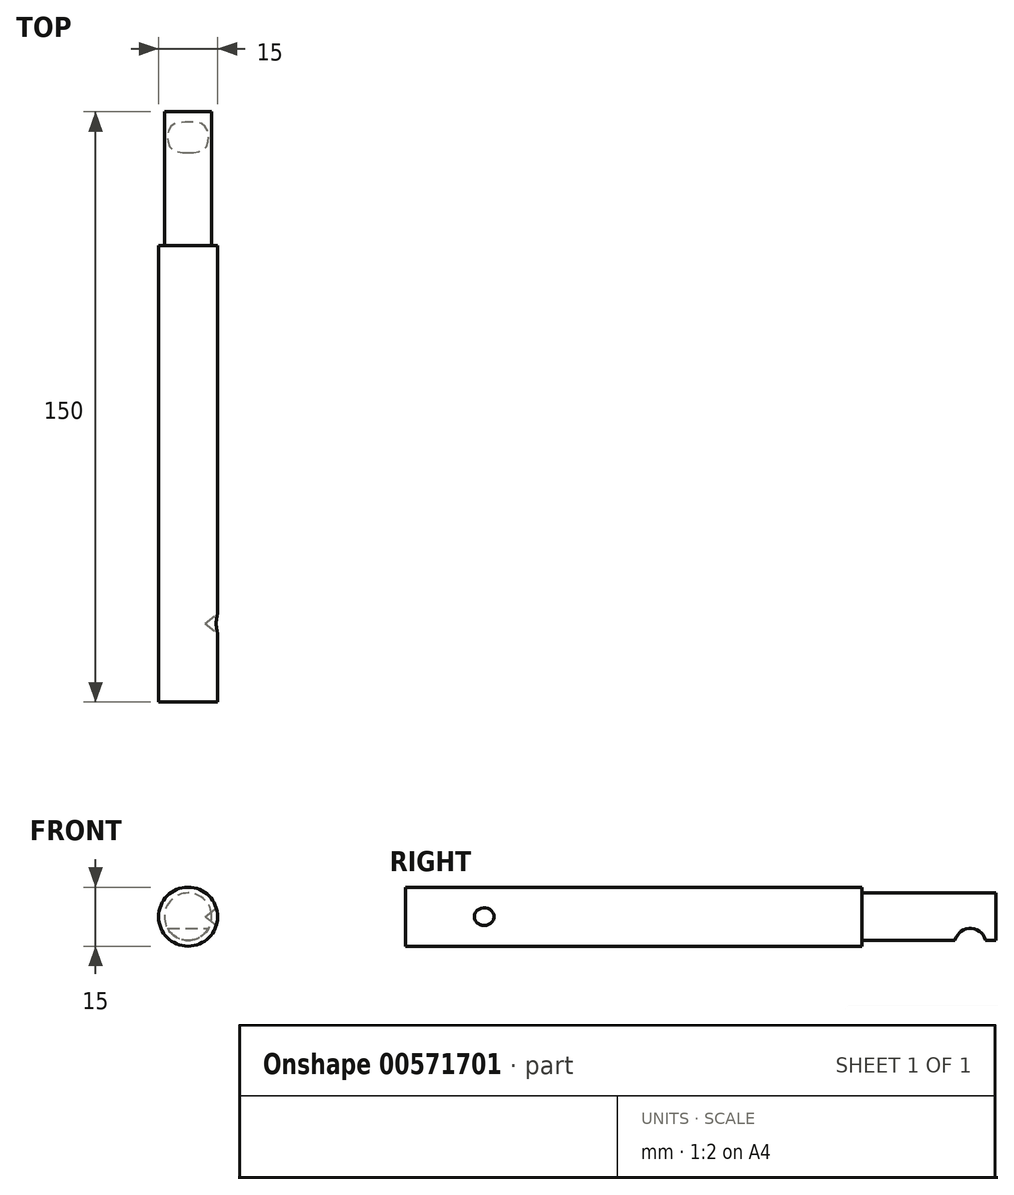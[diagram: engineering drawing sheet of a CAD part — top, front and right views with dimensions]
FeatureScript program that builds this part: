
annotation { "Feature Type Name" : "Feature", "Feature Type Description" : "" }
export const myFeature = defineFeature(function(context is Context, id is Id, definition is map)
    precondition{}
    {
        {
            var Q0;
            Q0=qCreatedBy(makeId("Top.planeOp"),FACE);
            var sketch = newSketch(context, id + "F0", { "sketchPlane" : qUnion([Q0])});
            skLineSegment(sketch, "E0", {"start": v(0, 0) * mm, "end": v(0, 150) * mm, "construction": true});
            skLineSegment(sketch, "E1", {"start": v(0, 0) * mm, "end": v(-7.5, 0) * mm});
            skLineSegment(sketch, "E2", {"start": v(-7.5, 0) * mm, "end": v(-7.5, 116) * mm});
            skLineSegment(sketch, "E3", {"start": v(-6, 116) * mm, "end": v(-6, 150) * mm});
            skLineSegment(sketch, "E4", {"start": v(-6, 150) * mm, "end": v(0, 150) * mm});
            skLineSegment(sketch, "E5", {"start": v(-6, 116) * mm, "end": v(-7.5, 116) * mm});
            skLineSegment(sketch, "E6", {"start": v(0, 150) * mm, "end": v(0, 0) * mm});
            skSolve(sketch);
        }
        {
            var Q0;
            Q0=makeQuery(id+"F0.imprint","IMPRINT",FACE,{"disambiguationData":[TD([[makeQuery(id+"F0.imprint","IMPRINT",EDGE,{"derivedFrom":sQuery(id+"F0.wireOp",EDGE,"E1")}),-1.0]])]});
            var Q1;
            Q1=sQuery(id+"F0.wireOp",EDGE,"E6");
            revolve(context, id + "F1", {"entities" : qUnion([Q0]), "axis" : qUnion([Q1]), "revolveType" : RevolveType.FULL});
        }
        {
            var Q0;
            Q0=qCreatedBy(makeId("Top.planeOp"),FACE);
            var sketch = newSketch(context, id + "F2", { "sketchPlane" : qUnion([Q0])});
            skLineSegment(sketch, "E7", {"start": v(9.37, 16) * mm, "end": v(4.37, 20) * mm});
            skLineSegment(sketch, "E8", {"start": v(4.37, 20) * mm, "end": v(9.37, 20) * mm});
            skLineSegment(sketch, "E9", {"start": v(9.37, 20) * mm, "end": v(9.37, 16) * mm});
            skLineSegment(sketch, "E10", {"start": v(4.37, 20) * mm, "end": v(19.8, 20) * mm, "construction": true});
            skSolve(sketch);
        }
        {
            var Q0;
            Q0=makeQuery(id+"F2.imprint","IMPRINT",FACE,{"disambiguationData":[TD([[makeQuery(id+"F2.imprint","IMPRINT",EDGE,{"derivedFrom":sQuery(id+"F2.wireOp",EDGE,"E7")}),-1.0]])]});
            var Q1;
            Q1=sQuery(id+"F2.wireOp",EDGE,"E10");
            revolve(context, id + "F3", {"operationType" : NewBodyOperationType.REMOVE, "entities" : qUnion([Q0]), "axis" : qUnion([Q1]), "revolveType" : RevolveType.FULL, "oppositeDirection" : true});
        }
        {
            var Q0;
            Q0=qCreatedBy(makeId("Right.planeOp"),FACE);
            var sketch = newSketch(context, id + "F4", { "sketchPlane" : qUnion([Q0])});
            skCircle(sketch, "E11", {"center": v(143.5, -7) * mm, "radius": 4 * mm});
            skLineSegment(sketch, "E12", {"start": v(148.02, 0) * mm, "end": v(123.1, 0) * mm, "construction": true});
            skSolve(sketch);
        }
        {
            var Q0;
            Q0=makeQuery(id+"F4.imprint","IMPRINT",FACE,{"disambiguationData":[TD([[makeQuery(id+"F4.imprint","IMPRINT",EDGE,{"derivedFrom":sQuery(id+"F4.wireOp",EDGE,"E11")}),1.0]])]});
            extrude(context, id + "F5", {"entities" : qUnion([Q0]), "operationType" : NewBodyOperationType.REMOVE, "endBound" : BoundingType.SYMMETRIC, "oppositeDirection" : true, "depth" : 25 * mm, "offsetDistance" : 25 * mm});
        }
    });
